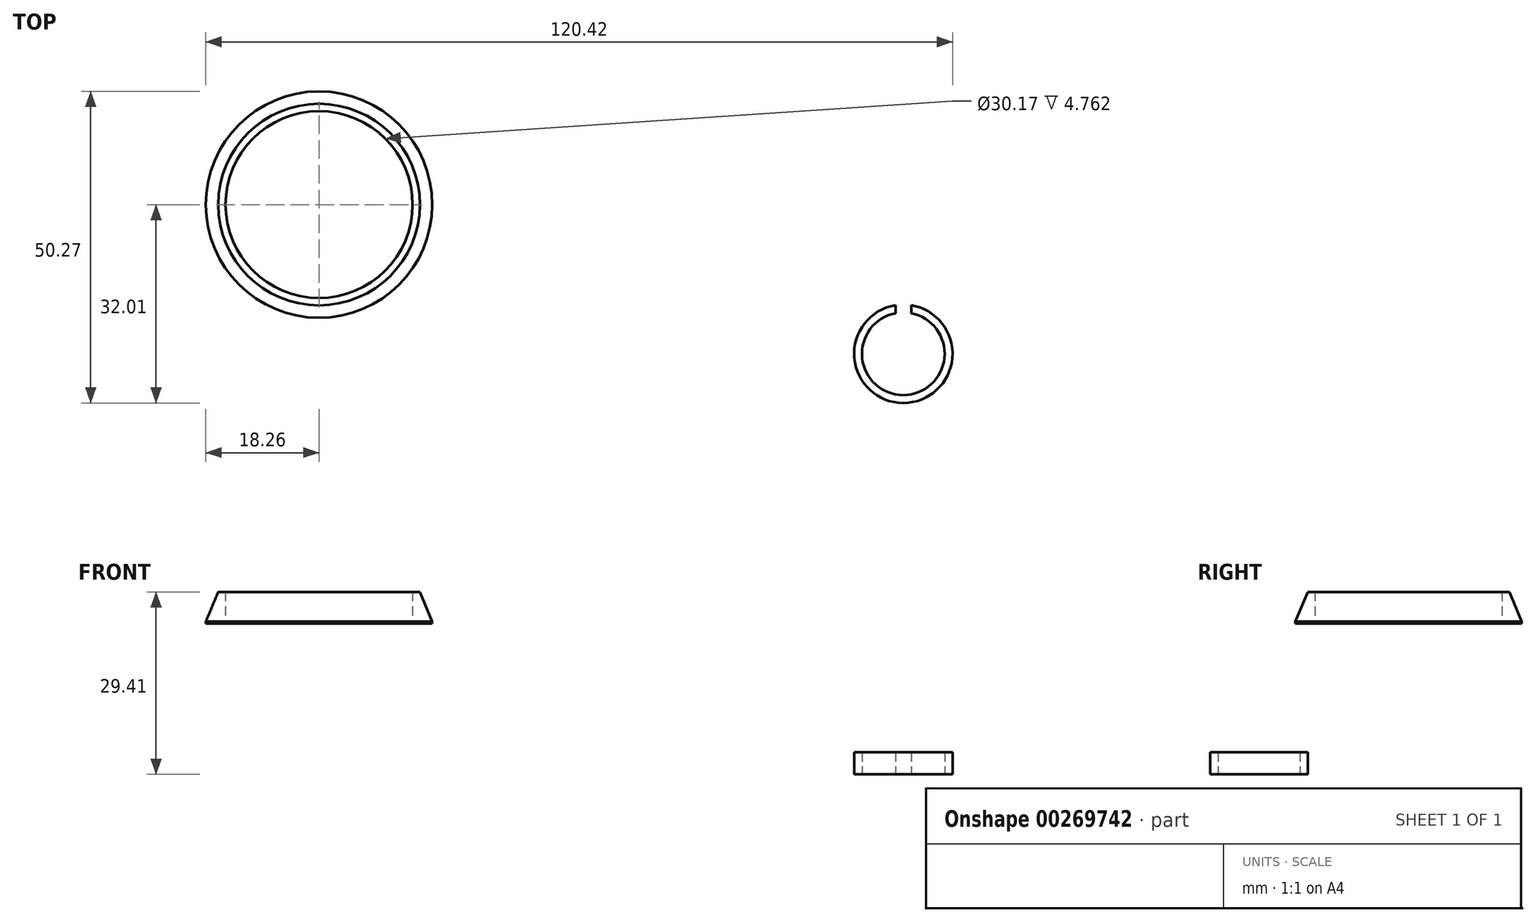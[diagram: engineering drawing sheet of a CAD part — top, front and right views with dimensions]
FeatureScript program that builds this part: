
annotation { "Feature Type Name" : "Feature", "Feature Type Description" : "" }
export const myFeature = defineFeature(function(context is Context, id is Id, definition is map)
    precondition{}
    {
        {
            var Q0;
            Q0=qCreatedBy(makeId("Front.planeOp"),FACE);
            var sketch = newSketch(context, id + "F0", { "sketchPlane" : qUnion([Q0])});
            skArc(sketch, "E0", {"start": v(18.26, 24.3) * mm, "mid": v(16.67, 24.49) * mm, "end": v(15.08, 24.65) * mm});
            skLineSegment(sketch, "E1", {"start": v(0, 25.4) * mm, "end": v(0, 37.6) * mm});
            skLineSegment(sketch, "E2", {"start": v(15.08, 24.65) * mm, "end": v(15.08, 29.41) * mm});
            skLineSegment(sketch, "E3", {"start": v(18.26, 29.41) * mm, "end": v(18.26, 24.3) * mm});
            skLineSegment(sketch, "E4", {"start": v(15.08, 29.41) * mm, "end": v(18.26, 29.41) * mm});
            skPoint(sketch, "E5.start.orphan", {"position": v(18.26, 0) * mm});
            skPoint(sketch, "E6.end.orphan", {"position": v(15.08, 0) * mm});
            skPoint(sketch, "E6.start.orphan", {"position": v(0, 0) * mm});
            skSolve(sketch);
        }
        {
            var Q0;
            Q0 = qSketchRegion(id + "F0", true);
            var Q1;
            Q1=sQuery(id+"F0.wireOp",EDGE,"E1");
            revolve(context, id + "F1", {"entities" : qUnion([Q0]), "axis" : qUnion([Q1]), "revolveType" : RevolveType.FULL});
        }
        {
            var Q0;
            Q0=makeQuery(id+"F1.opRevolve","SWEPT_EDGE",EDGE,{"disambiguationData":[OSD([sQuery(id+"F0.wireOp",EDGE,"E3"),sQuery(id+"F0.wireOp",EDGE,"E4")])]});
            chamfer(context, id + "F2", {"entities" : qUnion([Q0]), "chamferType" : ChamferType.TWO_OFFSETS, "width1" : 4.76 * mm, "oppositeDirection" : false, "width2" : 2 * mm, "tangentPropagation" : true});
        }
        {
            var Q0;
            Q0=qCreatedBy(makeId("Top.planeOp"), FACE);
            var sketch = newSketch(context, id + "F3", { "sketchPlane" : qUnion([Q0])});
            skArc(sketch, "E7", {"start": v(92.95, -16.24) * mm, "mid": v(94.22, -32.01) * mm, "end": v(95.49, -16.24) * mm});
            skArc(sketch, "E8", {"start": v(92.95, -17.53) * mm, "mid": v(94.22, -30.74) * mm, "end": v(95.49, -17.53) * mm});
            skLineSegment(sketch, "E9.left", {"start": v(95.49, -16.24) * mm, "end": v(95.49, -17.53) * mm});
            skLineSegment(sketch, "E9.right", {"start": v(92.95, -16.24) * mm, "end": v(92.95, -17.53) * mm});
            skPoint(sketch, "E9.bottom.end.orphan", {"position": v(92.95, -13.75) * mm});
            skPoint(sketch, "E10.orphan", {"position": v(95.49, -13.75) * mm});
            skPoint(sketch, "E9.top.end.orphan", {"position": v(92.95, -34.4) * mm});
            skPoint(sketch, "E9.top.start.orphan", {"position": v(95.49, -34.4) * mm});
            skSolve(sketch);
        }
        {
            var Q0;
            Q0 = qSketchRegion(id + "F3", true);
            extrude(context, id + "F4", {"entities" : qUnion([Q0]), "domain" : OperationDomain.MODEL, "flatOperationType" : FlatOperationType.REMOVE, "depth" : 3.56 * mm, "offsetDistance" : 25.4 * mm});
        }
    });
